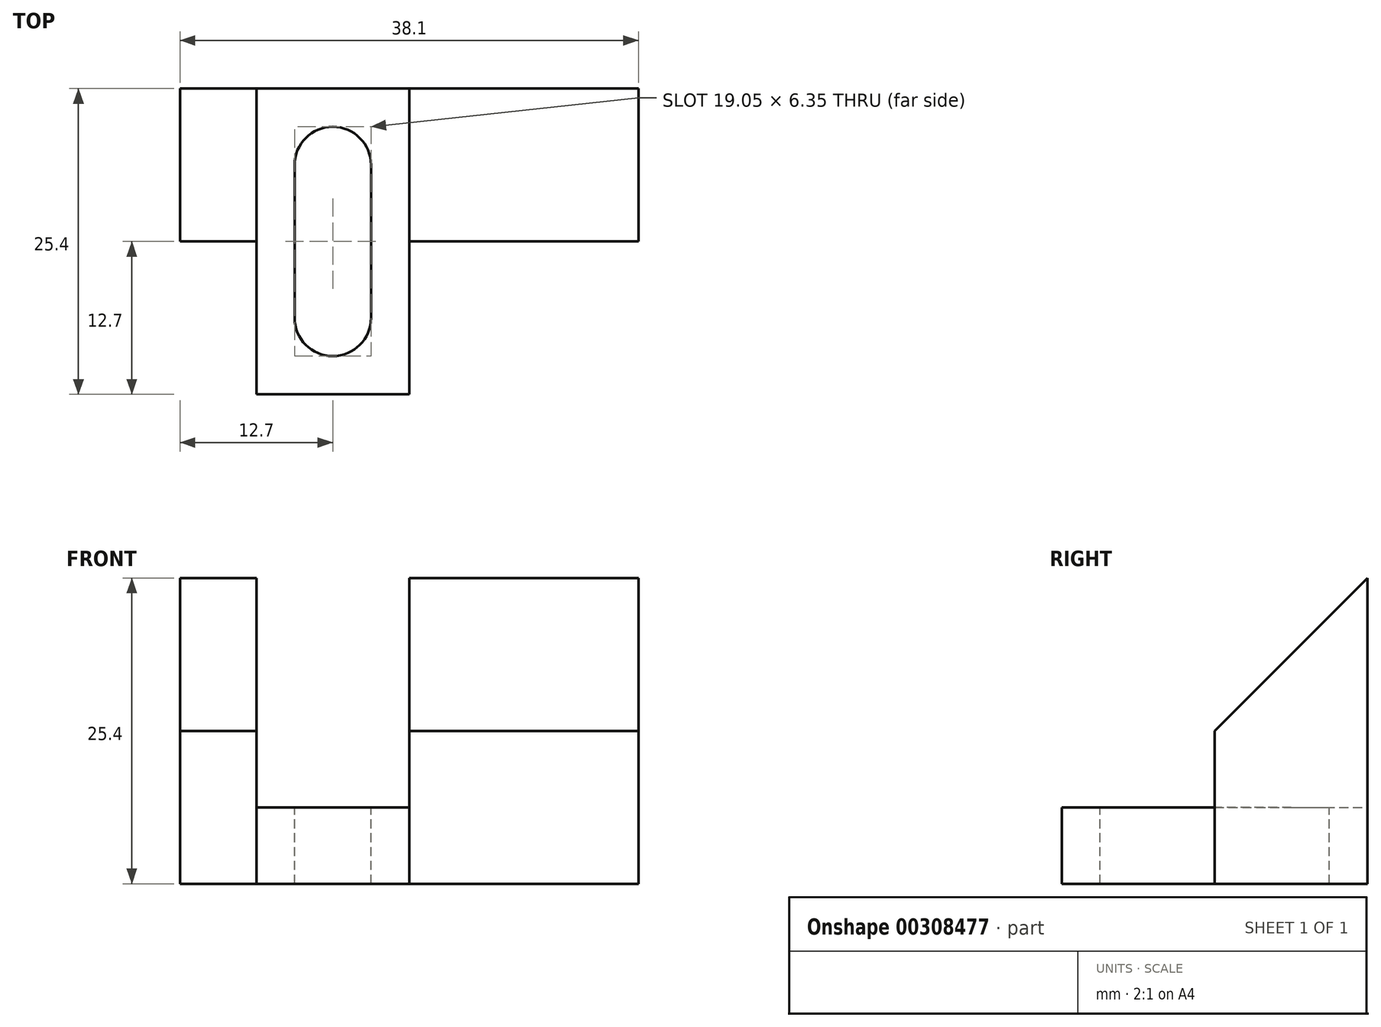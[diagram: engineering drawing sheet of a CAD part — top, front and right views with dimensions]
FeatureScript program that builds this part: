
annotation { "Feature Type Name" : "Feature", "Feature Type Description" : "" }
export const myFeature = defineFeature(function(context is Context, id is Id, definition is map)
    precondition{}
    {
        {
            var Q0;
            Q0=qCreatedBy(makeId("Front.planeOp"),FACE);
            var sketch = newSketch(context, id + "F0", { "sketchPlane" : qUnion([Q0])});
            skLineSegment(sketch, "E0", {"start": v(0, 0) * mm, "end": v(0, 25.4) * mm});
            skLineSegment(sketch, "E1", {"start": v(0, 25.4) * mm, "end": v(38.1, 25.4) * mm});
            skLineSegment(sketch, "E2", {"start": v(38.1, 25.4) * mm, "end": v(38.1, 0) * mm});
            skLineSegment(sketch, "E3", {"start": v(38.1, 0) * mm, "end": v(0, 0) * mm});
            skSolve(sketch);
        }
        {
            var Q0;
            Q0 = qSketchRegion(id + "F0", true);
            extrude(context, id + "F1", {"entities" : qUnion([Q0]), "depth" : 25.4 * mm});
        }
        {
            var Q0;
            Q0=makeQuery(id+"F1.opExtrude","SWEPT_FACE",FACE,{"disambiguationData":[OSD([sQuery(id+"F0.wireOp",EDGE,"E1")])]});
            var sketch = newSketch(context, id + "F2", { "sketchPlane" : qUnion([Q0])});
            skLineSegment(sketch, "E4", {"start": v(0, -25.4) * mm, "end": v(0, 0) * mm, "construction": true});
            skLineSegment(sketch, "E5", {"start": v(0, 0) * mm, "end": v(38.1, 0) * mm, "construction": true});
            skLineSegment(sketch, "E6", {"start": v(38.1, 0) * mm, "end": v(38.1, -25.4) * mm, "construction": true});
            skLineSegment(sketch, "E7", {"start": v(38.1, -25.4) * mm, "end": v(0, -25.4) * mm, "construction": true});
            skLineSegment(sketch, "E8", {"start": v(6.35, -25.4) * mm, "end": v(6.35, 0) * mm});
            skLineSegment(sketch, "E9", {"start": v(6.35, 0) * mm, "end": v(19.05, 0) * mm});
            skLineSegment(sketch, "E10", {"start": v(19.05, 0) * mm, "end": v(19.05, -25.4) * mm});
            skLineSegment(sketch, "E11", {"start": v(19.05, -25.4) * mm, "end": v(6.35, -25.4) * mm});
            skSolve(sketch);
        }
        {
            var Q0;
            Q0 = qSketchRegion(id + "F2", true);
            extrude(context, id + "F3", {"entities" : qUnion([Q0]), "operationType" : NewBodyOperationType.REMOVE, "endBound" : BoundingType.THROUGH_ALL, "oppositeDirection" : true, "depth" : 25.4 * mm});
        }
        {
            var Q0;
            Q0=makeQuery(id+"F1.opExtrude","SWEPT_FACE",FACE,{"disambiguationData":[OSD([sQuery(id+"F0.wireOp",EDGE,"E2")])]});
            var sketch = newSketch(context, id + "F4", { "sketchPlane" : qUnion([Q0])});
            skLineSegment(sketch, "E12", {"start": v(-25.4, 0) * mm, "end": v(0, 25.4) * mm});
            skLineSegment(sketch, "E13", {"start": v(0, 25.4) * mm, "end": v(-25.4, 25.4) * mm});
            skLineSegment(sketch, "E14", {"start": v(-25.4, 25.4) * mm, "end": v(-25.4, 0) * mm});
            skSolve(sketch);
        }
        {
            var Q0;
            Q0 = qSketchRegion(id + "F4", true);
            extrude(context, id + "F5", {"entities" : qUnion([Q0]), "operationType" : NewBodyOperationType.REMOVE, "endBound" : BoundingType.THROUGH_ALL, "oppositeDirection" : true, "depth" : 25.4 * mm});
        }
        {
            var Q0;
            Q0=makeQuery(id+"F3.boolean.opBoolean","COPY",FACE,{"derivedFrom":makeQuery(id+"F3.opExtrude","SWEPT_FACE",FACE,{"disambiguationData":[OSD([sQuery(id+"F2.wireOp",EDGE,"E8")])]})});
            var sketch = newSketch(context, id + "F6", { "sketchPlane" : qUnion([Q0])});
            skLineSegment(sketch, "E15", {"start": v(-25.4, 0) * mm, "end": v(0, 25.4) * mm});
            skLineSegment(sketch, "E16", {"start": v(0, 25.4) * mm, "end": v(-25.4, 25.4) * mm});
            skLineSegment(sketch, "E17", {"start": v(-25.4, 25.4) * mm, "end": v(-25.4, 0) * mm});
            skSolve(sketch);
        }
        {
            var Q0;
            Q0 = qSketchRegion(id + "F6", true);
            extrude(context, id + "F7", {"entities" : qUnion([Q0]), "operationType" : NewBodyOperationType.REMOVE, "endBound" : BoundingType.THROUGH_ALL, "oppositeDirection" : true, "depth" : 25.4 * mm});
        }
        {
            var Q0;
            Q0=makeQuery(id+"F1.opExtrude","SWEPT_FACE",FACE,{"disambiguationData":[OSD([sQuery(id+"F0.wireOp",EDGE,"E2")])]});
            var sketch = newSketch(context, id + "F8", { "sketchPlane" : qUnion([Q0])});
            skLineSegment(sketch, "E18", {"start": v(-12.7, 0) * mm, "end": v(-12.7, 12.7) * mm});
            skLineSegment(sketch, "E19", {"start": v(-12.7, 12.7) * mm, "end": v(-25.4, 0) * mm});
            skLineSegment(sketch, "E20", {"start": v(-25.4, 0) * mm, "end": v(-12.7, 0) * mm});
            skSolve(sketch);
        }
        {
            var Q0;
            Q0 = qSketchRegion(id + "F8", true);
            extrude(context, id + "F9", {"entities" : qUnion([Q0]), "operationType" : NewBodyOperationType.REMOVE, "endBound" : BoundingType.THROUGH_ALL, "oppositeDirection" : true, "depth" : 25.4 * mm});
        }
        {
            var Q0;
            Q0=qCreatedBy(makeId("Top.planeOp"),FACE);
            var sketch = newSketch(context, id + "F10", { "sketchPlane" : qUnion([Q0])});
            skLineSegment(sketch, "E21", {"start": v(6.35, 0) * mm, "end": v(19.05, 0) * mm});
            skLineSegment(sketch, "E22", {"start": v(19.05, 0) * mm, "end": v(19.05, -25.4) * mm});
            skLineSegment(sketch, "E23", {"start": v(19.05, -25.4) * mm, "end": v(6.35, -25.4) * mm});
            skLineSegment(sketch, "E24", {"start": v(6.35, -25.4) * mm, "end": v(6.35, 0) * mm});
            skSolve(sketch);
        }
        {
            var Q0;
            Q0 = qSketchRegion(id + "F10", true);
            extrude(context, id + "F11", {"entities" : qUnion([Q0]), "operationType" : NewBodyOperationType.ADD, "depth" : 6.35 * mm});
        }
        {
            var Q0;
            Q0=makeQuery(id+"F11.opExtrude","CAP_FACE",FACE,{"disambiguationData":[OSD([sQuery(id+"F10.wireOp",EDGE,"E21"),sQuery(id+"F10.wireOp",EDGE,"E22"),sQuery(id+"F10.wireOp",EDGE,"E23"),sQuery(id+"F10.wireOp",EDGE,"E24")])],"isStart":false});
            var sketch = newSketch(context, id + "F12", { "sketchPlane" : qUnion([Q0])});
            skLineSegment(sketch, "E25", {"start": v(6.35, 0) * mm, "end": v(19.05, 0) * mm, "construction": true});
            skLineSegment(sketch, "E26", {"start": v(19.05, 0) * mm, "end": v(19.05, -25.4) * mm, "construction": true});
            skLineSegment(sketch, "E27", {"start": v(19.05, -25.4) * mm, "end": v(6.35, -25.4) * mm, "construction": true});
            skLineSegment(sketch, "E28", {"start": v(6.35, -25.4) * mm, "end": v(6.35, 0) * mm, "construction": true});
            skLineSegment(sketch, "E29", {"start": v(12.7, 0) * mm, "end": v(12.7, -25.4) * mm, "construction": true});
            skArc(sketch, "E30", {"start": v(15.88, -6.35) * mm, "mid": v(12.7, -3.18) * mm, "end": v(9.53, -6.35) * mm});
            skArc(sketch, "E31", {"start": v(9.53, -19.05) * mm, "mid": v(12.7, -22.23) * mm, "end": v(15.88, -19.05) * mm});
            skLineSegment(sketch, "E32", {"start": v(9.53, -6.35) * mm, "end": v(9.53, -19.05) * mm});
            skLineSegment(sketch, "E33", {"start": v(15.88, -6.35) * mm, "end": v(15.88, -19.05) * mm});
            skLineSegment(sketch, "E34", {"start": v(6.35, 0) * mm, "end": v(12.7, -6.35) * mm, "construction": true});
            skLineSegment(sketch, "E35", {"start": v(19.05, 0) * mm, "end": v(12.7, -6.35) * mm, "construction": true});
            skLineSegment(sketch, "E36", {"start": v(6.35, -25.4) * mm, "end": v(12.7, -19.05) * mm, "construction": true});
            skLineSegment(sketch, "E37", {"start": v(19.05, -25.4) * mm, "end": v(12.7, -19.05) * mm, "construction": true});
            skSolve(sketch);
        }
        {
            var Q0;
            Q0 = qSketchRegion(id + "F12", true);
            extrude(context, id + "F13", {"entities" : qUnion([Q0]), "operationType" : NewBodyOperationType.REMOVE, "endBound" : BoundingType.THROUGH_ALL, "oppositeDirection" : true, "depth" : 25.4 * mm});
        }
    });
